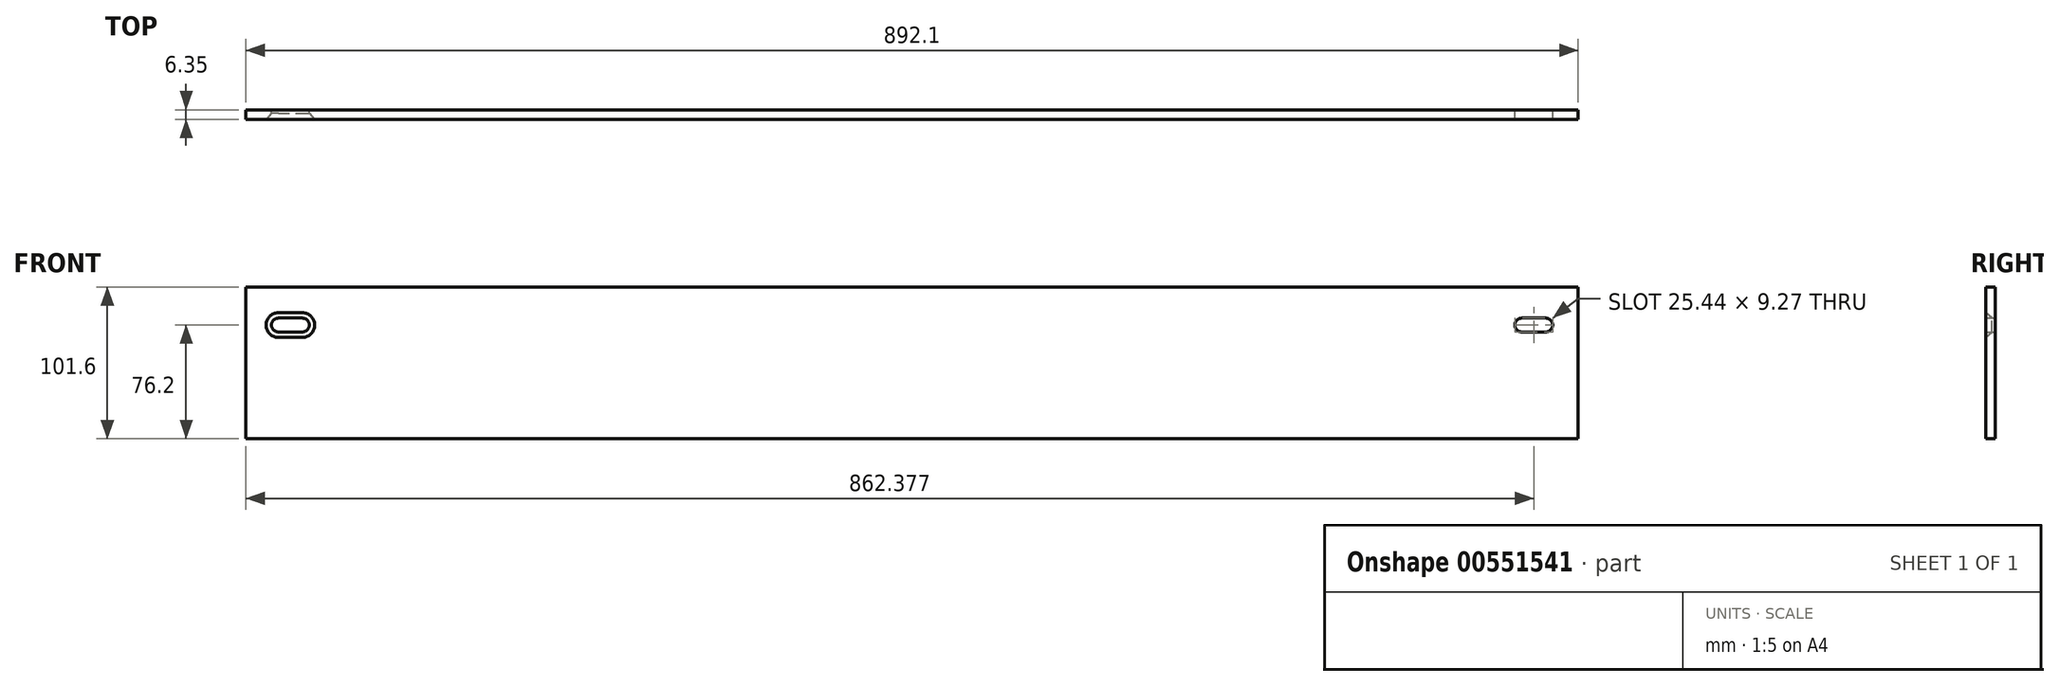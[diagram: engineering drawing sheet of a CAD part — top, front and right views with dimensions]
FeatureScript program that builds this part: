
annotation { "Feature Type Name" : "Feature", "Feature Type Description" : "" }
export const myFeature = defineFeature(function(context is Context, id is Id, definition is map)
    precondition{}
    {
        {
            var Q0;
            Q0=qCreatedBy(makeId("Front.planeOp"),FACE);
            var sketch = newSketch(context, id + "F0", { "sketchPlane" : qUnion([Q0])});
            skLineSegment(sketch, "E0", {"start": v(446.05, 50.8) * mm, "end": v(446.05, -50.8) * mm});
            skLineSegment(sketch, "E1", {"start": v(-446.05, 50.8) * mm, "end": v(446.05, 50.8) * mm});
            skLineSegment(sketch, "E2", {"start": v(-446.05, -50.8) * mm, "end": v(446.05, -50.8) * mm});
            skLineSegment(sketch, "E3", {"start": v(-446.05, 50.8) * mm, "end": v(-446.05, -50.8) * mm});
            skArc(sketch, "E4", {"start": v(424.41, 20.76) * mm, "mid": v(429.05, 25.4) * mm, "end": v(424.41, 30.04) * mm});
            skArc(sketch, "E5", {"start": v(408.24, 30.04) * mm, "mid": v(403.6, 25.4) * mm, "end": v(408.24, 20.76) * mm});
            skArc(sketch, "E6", {"start": v(-408.28, 20.76) * mm, "mid": v(-403.65, 25.4) * mm, "end": v(-408.28, 30.04) * mm});
            skArc(sketch, "E7", {"start": v(-424.37, 30.04) * mm, "mid": v(-429, 25.4) * mm, "end": v(-424.37, 20.76) * mm});
            skLineSegment(sketch, "E8", {"start": v(-408.28, 20.76) * mm, "end": v(-424.37, 20.76) * mm});
            skLineSegment(sketch, "E9", {"start": v(-424.37, 30.04) * mm, "end": v(-408.28, 30.04) * mm});
            skLineSegment(sketch, "E10", {"start": v(424.41, 20.76) * mm, "end": v(408.24, 20.76) * mm});
            skLineSegment(sketch, "E11", {"start": v(408.24, 30.04) * mm, "end": v(424.41, 30.04) * mm});
            skSolve(sketch);
        }
        {
            var Q0;
            Q0=makeQuery(id+"F0.imprint","IMPRINT",FACE,{"disambiguationData":[TD([[makeQuery(id+"F0.imprint","IMPRINT",EDGE,{"derivedFrom":sQuery(id+"F0.wireOp",EDGE,"E0")}),-1.0]])]});
            extrude(context, id + "F1", {"entities" : qUnion([Q0]), "depth" : 6.35 * mm, "offsetDistance" : 25.4 * mm});
        }
        {
            var Q0;
            Q0=makeQuery(id+"F1.opExtrude","CAP_EDGE",EDGE,{"disambiguationData":[OSD([sQuery(id+"F0.wireOp",EDGE,"E9")])],"isStart":false});
            chamfer(context, id + "F2", {"entities" : qUnion([Q0]), "chamferType" : ChamferType.OFFSET_ANGLE, "width" : 4.17 * mm, "oppositeDirection" : true, "angle" : 41 * degree, "tangentPropagation" : true});
        }
    });
